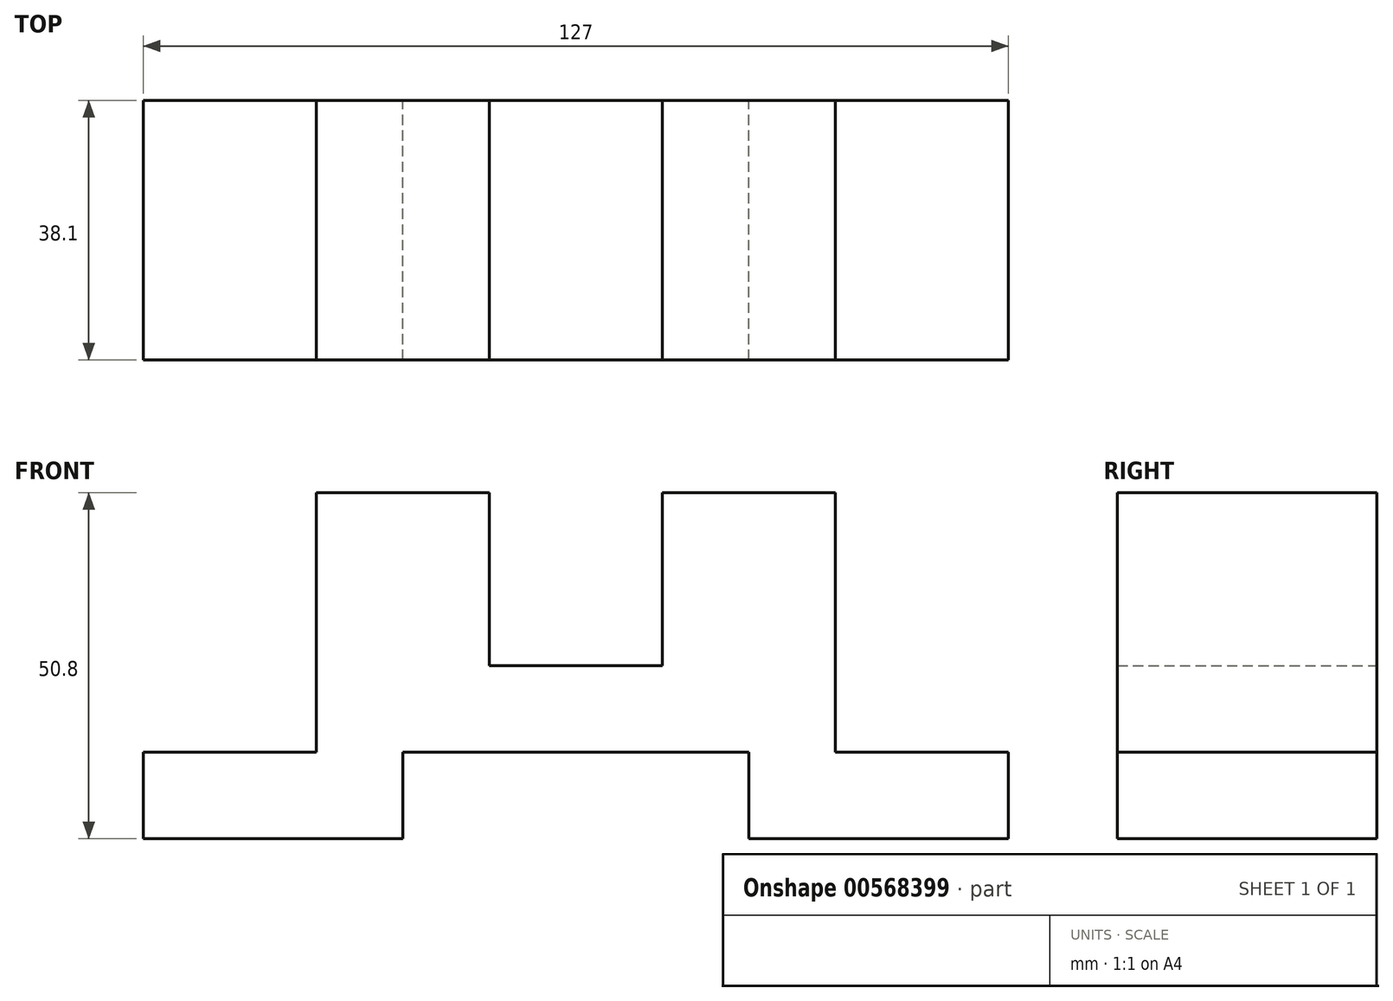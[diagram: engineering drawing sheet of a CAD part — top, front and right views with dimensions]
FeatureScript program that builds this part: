
annotation { "Feature Type Name" : "Feature", "Feature Type Description" : "" }
export const myFeature = defineFeature(function(context is Context, id is Id, definition is map)
    precondition{}
    {
        {
            var Q0;
            Q0=qCreatedBy(makeId("Front.planeOp"),FACE);
            var sketch = newSketch(context, id + "F0", { "sketchPlane" : qUnion([Q0])});
            skLineSegment(sketch, "E0", {"start": v(-76.62, -1.47) * mm, "end": v(-38.52, -1.47) * mm});
            skLineSegment(sketch, "E1", {"start": v(-38.52, -1.47) * mm, "end": v(-38.52, 11.23) * mm});
            skLineSegment(sketch, "E2", {"start": v(-38.52, 11.23) * mm, "end": v(12.28, 11.23) * mm});
            skLineSegment(sketch, "E3", {"start": v(12.28, 11.23) * mm, "end": v(12.28, -1.47) * mm});
            skLineSegment(sketch, "E4", {"start": v(12.28, -1.47) * mm, "end": v(50.38, -1.47) * mm});
            skLineSegment(sketch, "E5", {"start": v(50.38, -1.47) * mm, "end": v(50.38, 11.23) * mm});
            skLineSegment(sketch, "E6", {"start": v(50.38, 11.23) * mm, "end": v(24.98, 11.23) * mm});
            skLineSegment(sketch, "E7", {"start": v(24.98, 11.23) * mm, "end": v(24.98, 49.33) * mm});
            skLineSegment(sketch, "E8", {"start": v(24.98, 49.33) * mm, "end": v(-0.42, 49.33) * mm});
            skLineSegment(sketch, "E9", {"start": v(-0.42, 49.33) * mm, "end": v(-0.42, 23.93) * mm});
            skLineSegment(sketch, "E10", {"start": v(-0.42, 23.93) * mm, "end": v(-25.82, 23.93) * mm});
            skLineSegment(sketch, "E11", {"start": v(-25.82, 23.93) * mm, "end": v(-25.82, 49.33) * mm});
            skLineSegment(sketch, "E12", {"start": v(-51.22, 49.33) * mm, "end": v(-51.22, 11.23) * mm});
            skLineSegment(sketch, "E13", {"start": v(-51.22, 11.23) * mm, "end": v(-76.62, 11.23) * mm});
            skLineSegment(sketch, "E14", {"start": v(-51.22, 49.33) * mm, "end": v(-25.82, 49.33) * mm});
            skLineSegment(sketch, "E15", {"start": v(-76.62, 11.23) * mm, "end": v(-76.62, -1.47) * mm});
            skSolve(sketch);
        }
        {
            var Q0;
            Q0 = qSketchRegion(id + "F0", true);
            extrude(context, id + "F1", {"entities" : qUnion([Q0]), "depth" : 38.1 * mm, "offsetDistance" : 25.4 * mm});
        }
    });
